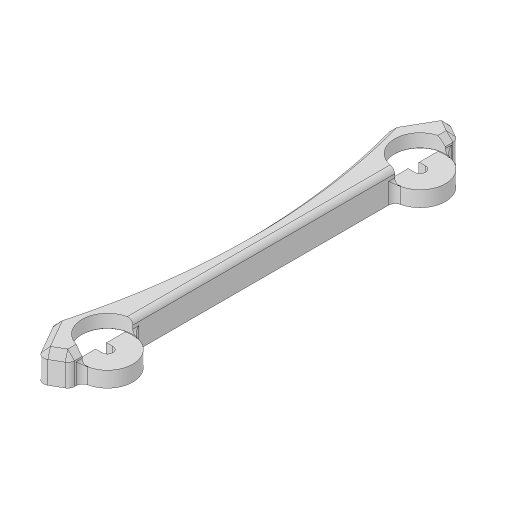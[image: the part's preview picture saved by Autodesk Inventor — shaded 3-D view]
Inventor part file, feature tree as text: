
AUTODESK INVENTOR PART (.ipt)
format: ipt  version: 2024.3 (Build 283343000, 343)  size: 1,416,192 bytes
history: native  units: mm
features: other x4, extrude x3, fillet x3, projected_geometry x2, sketch x1, chamfer x1
ambient origin geometry x8: Origin, YZ Plane, XZ Plane, XY Plane, X Axis, Y Axis, Z Axis, Center Point
bodies: Body1 (feature_tree)
feature tree (14):
  other  "實體1"
  other  "lite_bed_holder"
  other  "MeshFeature1"
  sketch  "草圖1"
  extrude  "擠出1"  Depth=3.25mm
  extrude  "擠出2"  Depth=15.0mm
  extrude  "擠出3"  Depth=13.6mm
  fillet  "圓角1"  Radius=7.5mm
  fillet  "圓角2"  [1 undecoded]
  chamfer  "倒角1"  Angle=90.0deg  [1 undecoded]
  fillet  "圓角3"  Radius=92.5mm
  projected_geometry  "投影迴路1"
  projected_geometry  "投影迴路2"
  other  "實體2"
note: 2 required parameter values undecoded (feature->parameter linkage not recoverable at this tier; creation-order binding heuristic only, values carry confidence <= 0.55)
